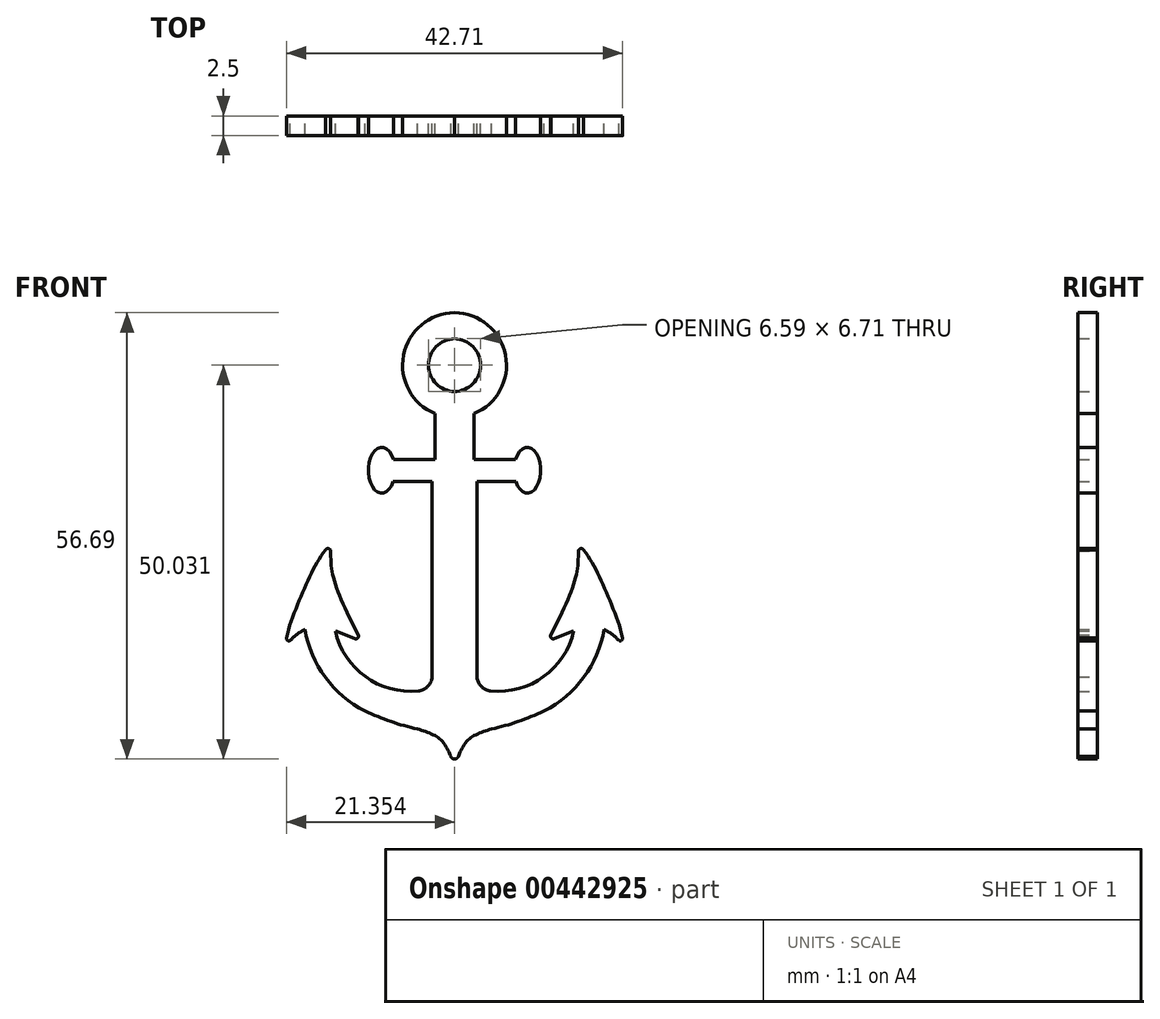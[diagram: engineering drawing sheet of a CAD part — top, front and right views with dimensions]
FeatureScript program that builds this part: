
annotation { "Feature Type Name" : "Feature", "Feature Type Description" : "" }
export const myFeature = defineFeature(function(context is Context, id is Id, definition is map)
    precondition{}
    {
        {
            var Q0;
            Q0=qCreatedBy(makeId("Front.planeOp"),FACE);
            var sketch = newSketch(context, id + "F0", { "sketchPlane" : qUnion([Q0])});
            skLineSegment(sketch, "E0", {"start": v(17.5, 38.25) * mm, "end": v(17.5, -15.99) * mm, "construction": true});
            skLineSegment(sketch, "E1", {"start": v(17.5, 38.25) * mm, "end": v(17.5, 50.76) * mm, "construction": true});
            skArc(sketch, "E2", {"start": v(17.5, 41.58) * mm, "mid": v(14.21, 38.22) * mm, "end": v(17.5, 34.86) * mm});
            skArc(sketch, "E3", {"start": v(17.5, 44.88) * mm, "mid": v(11.03, 39.48) * mm, "end": v(15.04, 32.06) * mm});
            skLineSegment(sketch, "E4", {"start": v(15.04, 32.06) * mm, "end": v(15.04, 26.25) * mm});
            skLineSegment(sketch, "E5", {"start": v(9.74, 26.25) * mm, "end": v(15.04, 26.25) * mm});
            skLineSegment(sketch, "E6", {"start": v(9.72, 23.44) * mm, "end": v(14.65, 23.44) * mm});
            skLineSegment(sketch, "E7", {"start": v(14.65, 23.44) * mm, "end": v(14.65, -1.41) * mm});
            skPoint(sketch, "E8.1.internal.orphan", {"position": v(14.65, -2.72) * mm});
            skPoint(sketch, "E8.3.internal.orphan", {"position": v(14.67, -1.41) * mm});
            skArc(sketch, "E9", {"start": v(12.92, -3.17) * mm, "mid": v(14.1, -2.6) * mm, "end": v(14.67, -1.41) * mm});
            skArc(sketch, "E10", {"start": v(2.36, 4.48) * mm, "mid": v(6.18, -1.35) * mm, "end": v(12.92, -3.17) * mm});
            skLineSegment(sketch, "E11", {"start": v(2.36, 4.48) * mm, "end": v(4.83, 3.48) * mm});
            skArc(sketch, "E12", {"start": v(4.83, 3.48) * mm, "mid": v(5.2, 3.57) * mm, "end": v(5.27, 3.95) * mm});
            skArc(sketch, "E13", {"start": v(1.78, 14.63) * mm, "mid": v(1.49, 14.91) * mm, "end": v(1.11, 14.76) * mm});
            skFitSpline(sketch, "E14", {"points": [v(1.11, 14.76) * mm, v(-1.53, 9.92) * mm, v(-3.85, 3.57) * mm], "startDerivative": vector(-7.02, -8.94) * mm, "endDerivative": vector(-2.6, -11.75) * mm});
            skArc(sketch, "E15", {"start": v(-3.85, 3.57) * mm, "mid": v(-3.71, 3.26) * mm, "end": v(-3.38, 3.24) * mm});
            skFitSpline(sketch, "E16", {"points": [v(-3.38, 3.24) * mm, v(-2.47, 4.07) * mm, v(-1.5, 4.64) * mm], "startDerivative": vector(1.73, 1.74) * mm, "endDerivative": vector(2.02, 1.07) * mm});
            skArc(sketch, "E17", {"start": v(-1.5, 4.64) * mm, "mid": v(1.1, -1.44) * mm, "end": v(6.14, -5.7) * mm});
            skArc(sketch, "E18", {"start": v(6.14, -5.7) * mm, "mid": v(9.41, -7.05) * mm, "end": v(12.82, -8) * mm});
            skFitSpline(sketch, "E19", {"points": [v(12.82, -8) * mm, v(14.03, -8.4) * mm, v(15.12, -8.9) * mm, v(15.98, -9.61) * mm, v(16.68, -10.72) * mm, v(17.03, -11.5) * mm], "startDerivative": vector(5.78, -1.86) * mm, "endDerivative": vector(1.73, -4.28) * mm});
            skArc(sketch, "E20", {"start": v(17.03, -11.5) * mm, "mid": v(17.21, -11.73) * mm, "end": v(17.5, -11.8) * mm});
            skEllipticalArc(sketch, "E21", {});
            skLineSegment(sketch, "E22", {"start": v(9.74, 26.25) * mm, "end": v(9.73, 26.25) * mm});
            skArc(sketch, "E23.MirrorCS", {"start": v(17.5, 44.88) * mm, "mid": v(23.98, 39.48) * mm, "end": v(19.97, 32.06) * mm});
            skArc(sketch, "E24.MirrorCS", {"start": v(17.5, 41.58) * mm, "mid": v(20.8, 38.22) * mm, "end": v(17.5, 34.86) * mm});
            skLineSegment(sketch, "E25.MirrorCS", {"start": v(19.97, 32.06) * mm, "end": v(19.97, 26.25) * mm});
            skLineSegment(sketch, "E26.MirrorCS", {"start": v(25.27, 26.25) * mm, "end": v(19.97, 26.25) * mm});
            skEllipticalArc(sketch, "E27.MirrorCS", {});
            skLineSegment(sketch, "E28.MirrorCS", {"start": v(25.3, 23.44) * mm, "end": v(20.36, 23.44) * mm});
            skLineSegment(sketch, "E29.MirrorCS", {"start": v(20.36, 23.44) * mm, "end": v(20.36, -1.41) * mm});
            skArc(sketch, "E30.MirrorCS", {"start": v(22.1, -3.17) * mm, "mid": v(20.9, -2.6) * mm, "end": v(20.34, -1.41) * mm});
            skArc(sketch, "E31.MirrorCS", {"start": v(32.64, 4.48) * mm, "mid": v(28.82, -1.35) * mm, "end": v(22.1, -3.17) * mm});
            skLineSegment(sketch, "E32.MirrorCS", {"start": v(32.64, 4.48) * mm, "end": v(30.18, 3.48) * mm});
            skArc(sketch, "E33.MirrorCS", {"start": v(30.18, 3.48) * mm, "mid": v(29.8, 3.57) * mm, "end": v(29.73, 3.95) * mm});
            skArc(sketch, "E34.MirrorCS", {"start": v(33.23, 14.63) * mm, "mid": v(33.52, 14.91) * mm, "end": v(33.9, 14.76) * mm});
            skFitSpline(sketch, "E35.MirrorCS", {"points": [v(33.9, 14.76) * mm, v(36.54, 9.92) * mm, v(38.86, 3.57) * mm], "startDerivative": vector(7.02, -8.94) * mm, "endDerivative": vector(2.6, -11.75) * mm});
            skArc(sketch, "E36.MirrorCS", {"start": v(38.86, 3.57) * mm, "mid": v(38.72, 3.26) * mm, "end": v(38.39, 3.24) * mm});
            skFitSpline(sketch, "E37.MirrorCS", {"points": [v(38.39, 3.24) * mm, v(37.48, 4.07) * mm, v(36.51, 4.64) * mm], "startDerivative": vector(-1.73, 1.74) * mm, "endDerivative": vector(-2.02, 1.07) * mm});
            skArc(sketch, "E38.MirrorCS", {"start": v(36.51, 4.64) * mm, "mid": v(33.91, -1.44) * mm, "end": v(28.86, -5.7) * mm});
            skFitSpline(sketch, "E39.MirrorCS", {"points": [v(22.19, -8) * mm, v(20.97, -8.4) * mm, v(19.89, -8.9) * mm, v(19.03, -9.61) * mm, v(18.32, -10.72) * mm, v(17.98, -11.5) * mm], "startDerivative": vector(-5.78, -1.86) * mm, "endDerivative": vector(-1.73, -4.28) * mm});
            skArc(sketch, "E40.MirrorCS", {"start": v(17.98, -11.5) * mm, "mid": v(17.8, -11.73) * mm, "end": v(17.5, -11.8) * mm});
            skArc(sketch, "E41.MirrorCS", {"start": v(28.86, -5.7) * mm, "mid": v(25.6, -7.05) * mm, "end": v(22.19, -8) * mm});
            skPoint(sketch, "E42.orphan", {"position": v(17.5, 31.56) * mm});
            skLineSegment(sketch, "E43", {"start": v(25.27, 26.25) * mm, "end": v(25.28, 26.25) * mm});
            skFitSpline(sketch, "E44", {"points": [v(5.27, 3.95) * mm, v(2.73, 9.36) * mm, v(1.89, 12.43) * mm, v(1.78, 14.63) * mm], "startDerivative": vector(-6.76, 13.38) * mm, "endDerivative": vector(-0.06, 8.28) * mm});
            skFitSpline(sketch, "E45.MirrorCS", {"points": [v(29.73, 3.95) * mm, v(32.28, 9.36) * mm, v(33.12, 12.43) * mm, v(33.23, 14.63) * mm], "startDerivative": vector(6.76, 13.38) * mm, "endDerivative": vector(0.06, 8.28) * mm});
            skLineSegment(sketch, "E46", {"start": v(15.04, 32.06) * mm, "end": v(19.97, 32.06) * mm});
            skLineSegment(sketch, "E47", {"start": v(9.72, 23.44) * mm, "end": v(9.74, 26.25) * mm});
            skLineSegment(sketch, "E48", {"start": v(25.3, 23.44) * mm, "end": v(25.28, 26.25) * mm});
            skLineSegment(sketch, "E49", {"start": v(32.64, 4.48) * mm, "end": v(36.51, 4.64) * mm});
            skLineSegment(sketch, "E50", {"start": v(14.67, -1.41) * mm, "end": v(20.36, -1.41) * mm});
            skLineSegment(sketch, "E51", {"start": v(-1.5, 4.64) * mm, "end": v(2.36, 4.48) * mm});
            skLineSegment(sketch, "E52", {"start": v(20.34, -1.41) * mm, "end": v(20.36, -1.41) * mm});
            skLineSegment(sketch, "E53", {"start": v(14.65, -1.41) * mm, "end": v(14.67, -1.41) * mm});
            const initialGuessF0  = {"E21": [0.008244960568845272, 0.024870822206139565, 0, 1, 0.0029189549386501312, 0.0016869629892020657, 5.206327264973328, 4.201301801492759], "E27.MirrorCS": [0.02676210645586252, 0.024870822206139568, 0, 1, 0.0029189549386501312, 0.0016869629892020657, 2.081883505686827, 1.0768580422062581]};
            skSetInitialGuess(sketch, initialGuessF0);
            skSolve(sketch);
        }
        {
            var Q0;
            Q0=makeQuery(id+"F0.imprint","IMPRINT",FACE,{"disambiguationData":[TD([[makeQuery(id+"F0.imprint","IMPRINT",EDGE,{"derivedFrom":sQuery(id+"F0.wireOp",EDGE,"E4")}),1.0]])]});
            var Q1;
            Q1=makeQuery(id+"F0.imprint","IMPRINT",FACE,{"disambiguationData":[TD([[makeQuery(id+"F0.imprint","IMPRINT",EDGE,{"derivedFrom":sQuery(id+"F0.wireOp",EDGE,"E27.MirrorCS")}),1.0]])]});
            var Q2;
            Q2=makeQuery(id+"F0.imprint","IMPRINT",FACE,{"disambiguationData":[TD([[makeQuery(id+"F0.imprint","IMPRINT",EDGE,{"derivedFrom":sQuery(id+"F0.wireOp",EDGE,"E2")}),-1.0]])]});
            var Q3;
            Q3=makeQuery(id+"F0.imprint","IMPRINT",FACE,{"disambiguationData":[TD([[makeQuery(id+"F0.imprint","IMPRINT",EDGE,{"derivedFrom":sQuery(id+"F0.wireOp",EDGE,"E21")}),1.0]])]});
            var Q4;
            Q4=makeQuery(id+"F0.imprint","IMPRINT",FACE,{"disambiguationData":[TD([[makeQuery(id+"F0.imprint","IMPRINT",EDGE,{"derivedFrom":sQuery(id+"F0.wireOp",EDGE,"E9")}),-1.0]])]});
            var Q5;
            Q5=makeQuery(id+"F0.imprint","IMPRINT",FACE,{"disambiguationData":[TD([[makeQuery(id+"F0.imprint","IMPRINT",EDGE,{"derivedFrom":sQuery(id+"F0.wireOp",EDGE,"E11")}),1.0]])]});
            var Q6;
            Q6=makeQuery(id+"F0.imprint","IMPRINT",FACE,{"disambiguationData":[TD([[makeQuery(id+"F0.imprint","IMPRINT",EDGE,{"derivedFrom":sQuery(id+"F0.wireOp",EDGE,"E32.MirrorCS")}),-1.0]])]});
            extrude(context, id + "F1", {"entities" : qUnion([Q0, Q1, Q2, Q3, Q4, Q5, Q6]), "depth" : 2.5 * mm});
        }
    });
